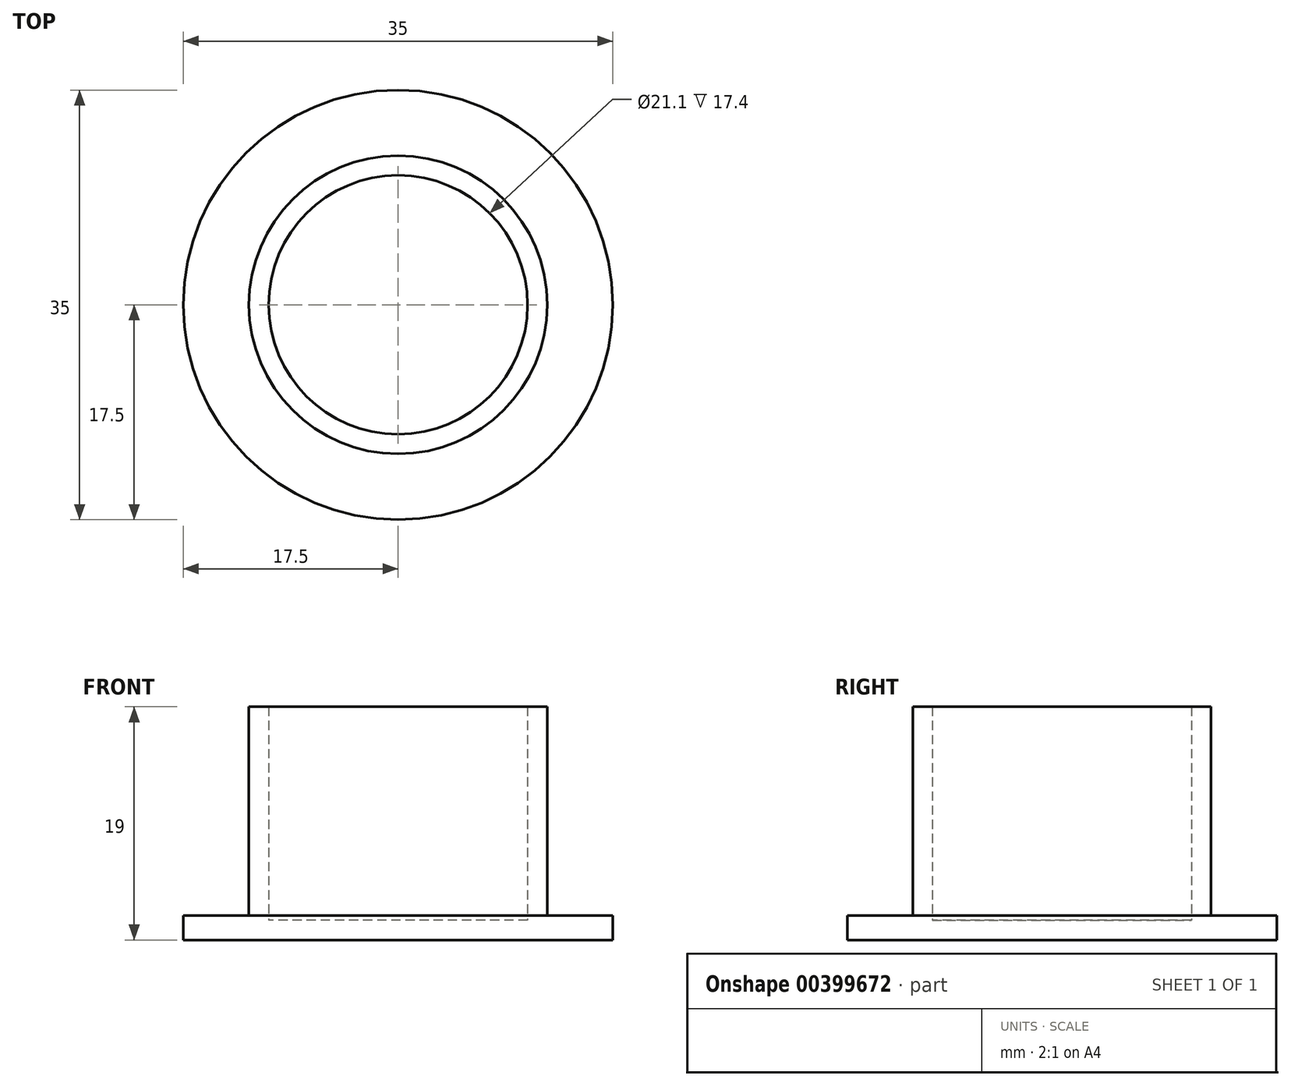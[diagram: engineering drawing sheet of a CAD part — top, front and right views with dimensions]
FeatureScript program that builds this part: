
annotation { "Feature Type Name" : "Feature", "Feature Type Description" : "" }
export const myFeature = defineFeature(function(context is Context, id is Id, definition is map)
    precondition{}
    {
        {
            var Q0;
            Q0=qCreatedBy(makeId("Top.planeOp"),FACE);
            var sketch = newSketch(context, id + "F0", { "sketchPlane" : qUnion([Q0])});
            skCircle(sketch, "E0", {"center": v(0, 0) * mm, "radius": 17.5 * mm});
            skSolve(sketch);
        }
        {
            var Q0;
            Q0 = qSketchRegion(id + "F0", true);
            extrude(context, id + "F1", {"entities" : qUnion([Q0]), "depth" : 2 * mm});
        }
        {
            var Q0;
            Q0=makeQuery(id+"F1.opExtrude","CAP_FACE",FACE,{"disambiguationData":[OSD([sQuery(id+"F0.wireOp",EDGE,"E0")])],"isStart":false});
            var sketch = newSketch(context, id + "F2", { "sketchPlane" : qUnion([Q0])});
            skCircle(sketch, "E1", {"center": v(0, 0) * mm, "radius": 12.15 * mm});
            skSolve(sketch);
        }
        {
            var Q0;
            Q0 = qSketchRegion(id + "F2", true);
            extrude(context, id + "F3", {"entities" : qUnion([Q0]), "operationType" : NewBodyOperationType.ADD, "depth" : 17 * mm});
        }
        {
            var Q0;
            Q0=makeQuery(id+"F3.opExtrude","CAP_FACE",FACE,{"disambiguationData":[OSD([sQuery(id+"F2.wireOp",EDGE,"E1")])],"isStart":false});
            shell(context, id + "F4", {"entities" : qUnion([Q0]), "thickness" : 1.6 * mm});
        }
    });
